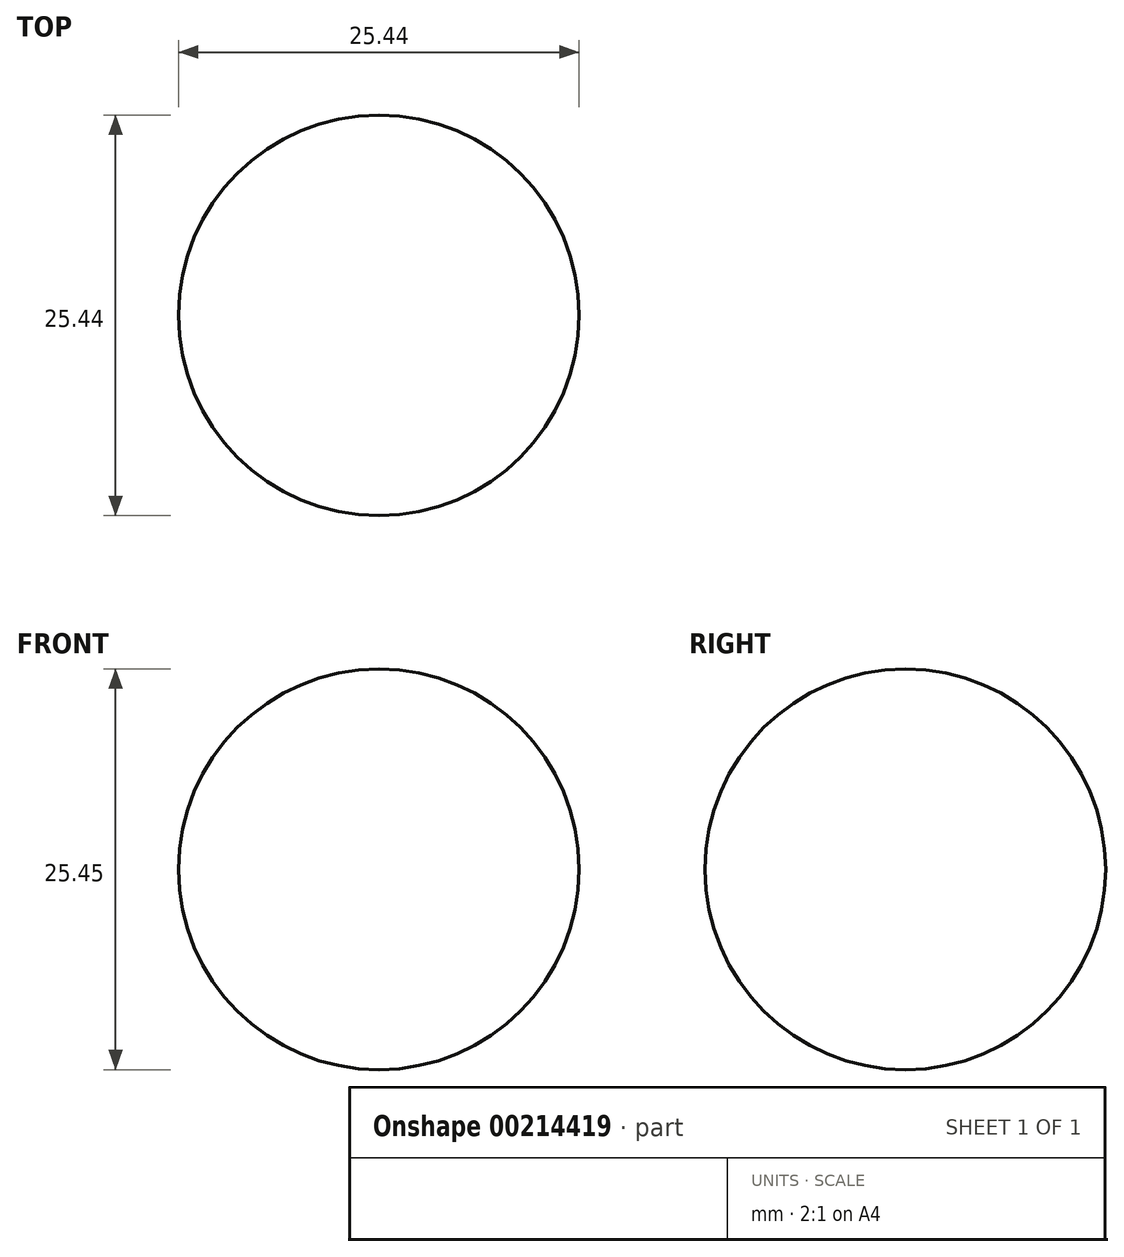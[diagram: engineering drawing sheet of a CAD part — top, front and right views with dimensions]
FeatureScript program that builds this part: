
annotation { "Feature Type Name" : "Feature", "Feature Type Description" : "" }
export const myFeature = defineFeature(function(context is Context, id is Id, definition is map)
    precondition{}
    {
        {
            var Q0;
            Q0=qCreatedBy(makeId("Front.planeOp"),FACE);
            var sketch = newSketch(context, id + "F0", { "sketchPlane" : qUnion([Q0])});
            skArc(sketch, "E0", {"start": v(0, 25.45) * mm, "mid": v(-12.72, 12.72) * mm, "end": v(0, 0) * mm});
            skLineSegment(sketch, "E1", {"start": v(0, 25.45) * mm, "end": v(0, 0) * mm});
            skSolve(sketch);
        }
        {
            var Q0;
            Q0 = qSketchRegion(id + "F0", true);
            var Q1;
            Q1=sQuery(id+"F0.wireOp",EDGE,"E1");
            revolve(context, id + "F1", {"entities" : qUnion([Q0]), "axis" : qUnion([Q1]), "revolveType" : RevolveType.FULL});
        }
    });
